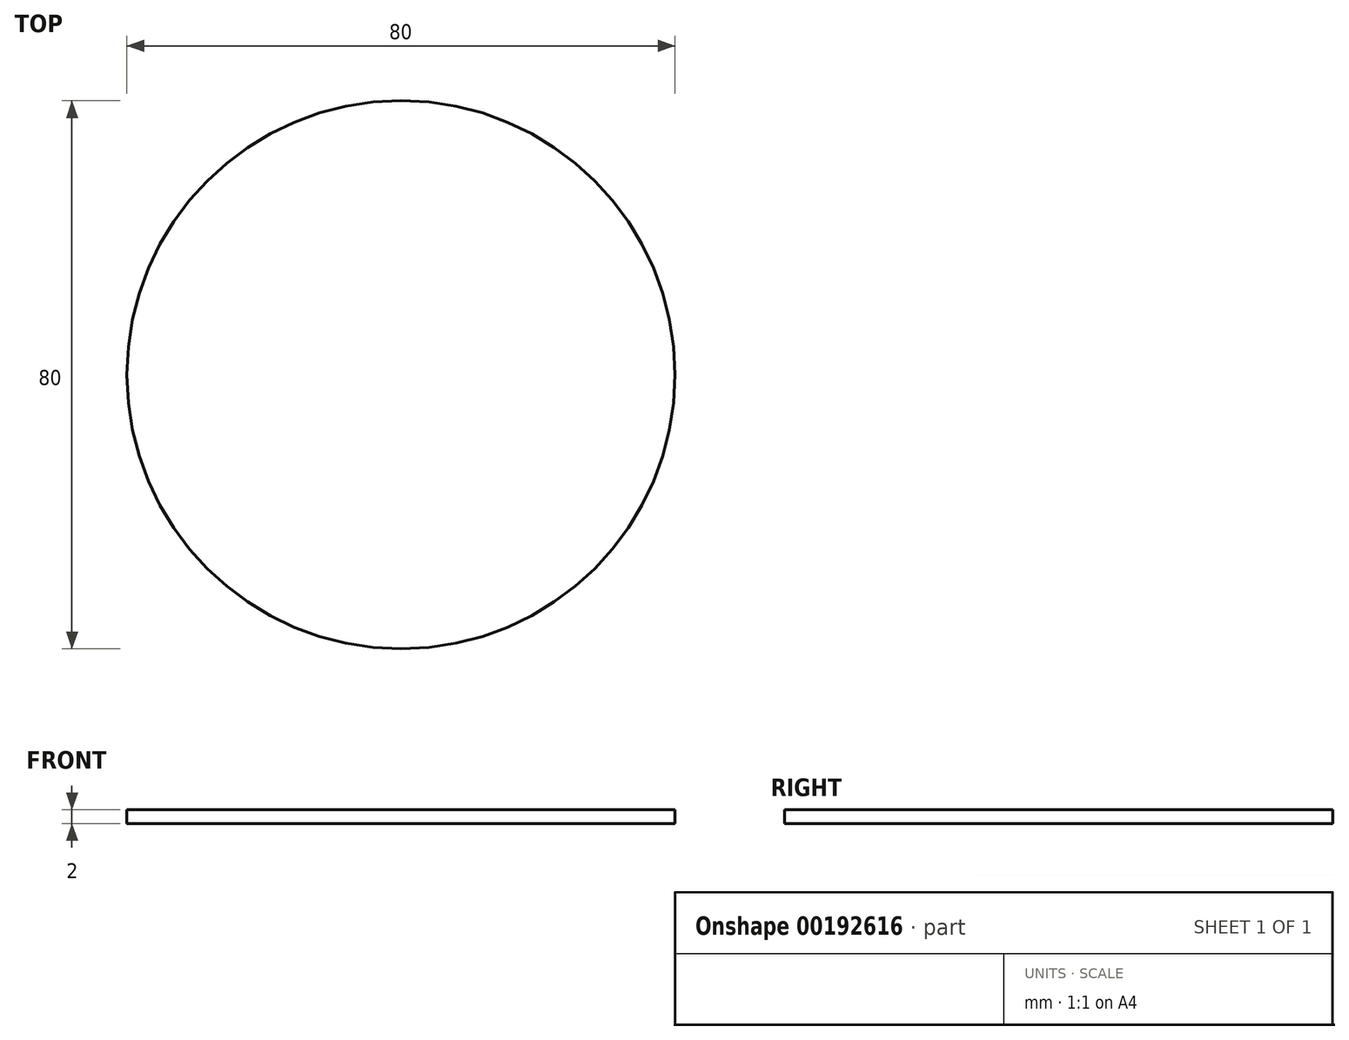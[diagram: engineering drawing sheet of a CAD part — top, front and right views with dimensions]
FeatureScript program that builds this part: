
annotation { "Feature Type Name" : "Feature", "Feature Type Description" : "" }
export const myFeature = defineFeature(function(context is Context, id is Id, definition is map)
    precondition{}
    {
        {
            var Q0;
            Q0=qCreatedBy(makeId("Top.planeOp"),FACE);
            var sketch = newSketch(context, id + "F0", { "sketchPlane" : qUnion([Q0])});
            skCircle(sketch, "E0", {"center": v(0, 0) * mm, "radius": 40 * mm});
            skSolve(sketch);
        }
        {
            var Q0;
            Q0=makeQuery(id+"F0.imprint","IMPRINT",FACE,{"disambiguationData":[TD([[makeQuery(id+"F0.imprint","IMPRINT",EDGE,{"derivedFrom":sQuery(id+"F0.wireOp",EDGE,"E0")}),1.0]])]});
            extrude(context, id + "F1", {"entities" : qUnion([Q0]), "depth" : 2 * mm});
        }
    });
